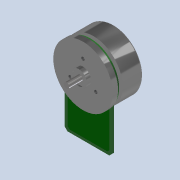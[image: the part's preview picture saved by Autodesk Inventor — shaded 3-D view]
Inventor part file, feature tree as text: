
AUTODESK INVENTOR PART (.ipt)
format: ipt  version: 2020.4 (Build 244396000, 396)  size: 229,888 bytes
history: native  units: mm
features: sketch x5, extrude x4, projected_geometry x2, other x1, revolve x1, fillet x1, hole x1, pattern_circular x1, chamfer x1
ambient origin geometry x8: Origin, YZ Plane, XZ Plane, XY Plane, X Axis, Y Axis, Z Axis, Center Point
bodies: Volumenkörper1 (feature_tree)
feature tree (17):
  other  "MaxonEC45-50W-MILE"
  revolve  "Umdrehung1"
  fillet  "Rundung1"  Radius=44.0mm
  extrude  "Extrusion1"  Depth=1.6mm
  hole  "Bohrung1"  [1 undecoded]
  pattern_circular  "Runde Anordnung1"  [2 undecoded]
  extrude  "Extrusion2"  Depth=0.01mm
  chamfer  "Fase1"  Distance=42.4mm
  extrude  "Extrusion3"  Depth=0.01mm
  extrude  "Extrusion4"  TaperAngle=90.0deg  [1 undecoded]
  sketch  "Skizze1"  dims[d1=4.0mm d2=1.6mm]
  sketch  "Skizze3"  dims[d3=2.1mm d4=22.6mm]
  sketch  "Skizze4"  dims[d5=43.4mm]
  sketch  "Sketch5"  dims[d6=12.0mm]
  projected_geometry  "Projected Loop1"
  sketch  "Sketch6"  dims[d7=4.0mm d8=3.2mm d9=20.2mm d10=42.4mm d11=36.5mm d12=90.0deg d13=1.0mm d14=1.0mm d15=1.0mm d16=0.0mm d17=11.0mm d18=2.459mm d19=6.0mm d20=4.0mm d21=2.0mm d22=90.0deg d23=3.9mm d24=20.594885mm d25=30.0mm d26=360.0deg d28=35.0mm d29=45.3mm d30=1.6mm d31=0.0mm d32=2.0mm d33=2.0mm d34=45.0deg d35=2.0mm d36=30.0mm d37=2.0mm d38=135.0deg d39=28.0mm d40=135.0deg d41=2.0mm d42=135.0deg d43=0.01mm d44=0.0mm d45=8.0mm d46=0.0mm]
  projected_geometry  "Projected Loop2"
note: 4 required parameter values undecoded (feature->parameter linkage not recoverable at this tier; creation-order binding heuristic only, values carry confidence <= 0.55)
